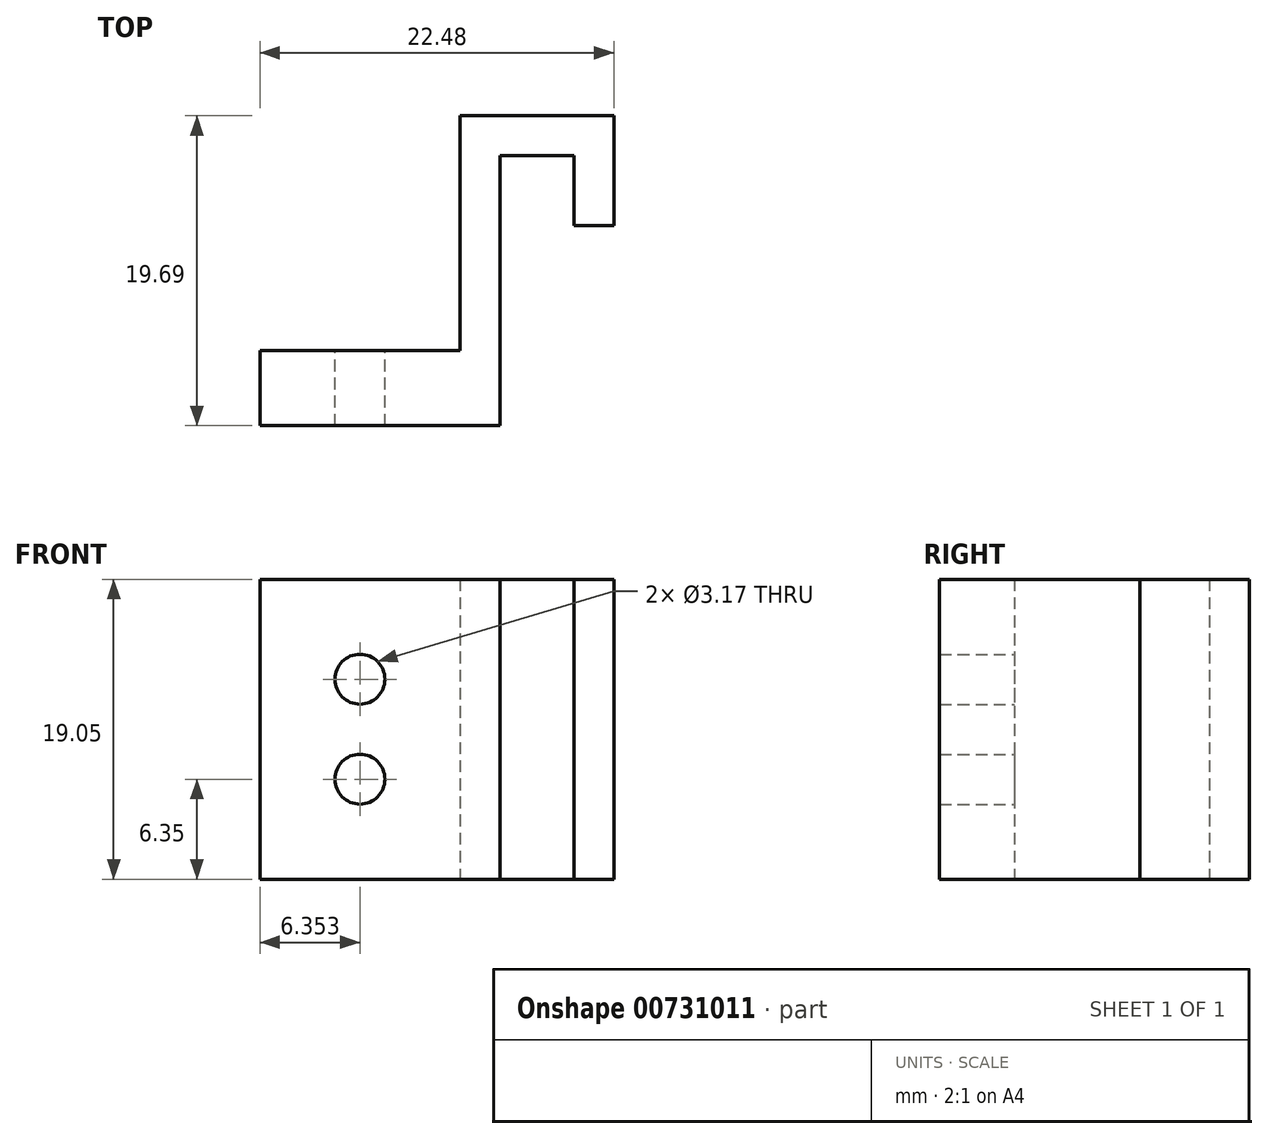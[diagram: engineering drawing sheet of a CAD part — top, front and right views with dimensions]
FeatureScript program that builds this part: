
annotation { "Feature Type Name" : "Feature", "Feature Type Description" : "" }
export const myFeature = defineFeature(function(context is Context, id is Id, definition is map)
    precondition{}
    {
        {
            var Q0;
            Q0=qCreatedBy(makeId("Top.planeOp"),FACE);
            var sketch = newSketch(context, id + "F0", { "sketchPlane" : qUnion([Q0])});
            skLineSegment(sketch, "E0.bottom", {"start": v(0, 0) * mm, "end": v(7.24, 0) * mm});
            skLineSegment(sketch, "E0.top", {"start": v(0, 2.54) * mm, "end": v(7.24, 2.54) * mm});
            skLineSegment(sketch, "E0.left", {"start": v(0, 0) * mm, "end": v(0, 2.54) * mm});
            skLineSegment(sketch, "E0.right", {"start": v(7.24, 0) * mm, "end": v(7.24, 2.54) * mm});
            skLineSegment(sketch, "E1.bottom", {"start": v(7.24, 0) * mm, "end": v(4.7, 0) * mm});
            skLineSegment(sketch, "E1.top", {"start": v(7.24, -4.42) * mm, "end": v(4.7, -4.42) * mm});
            skLineSegment(sketch, "E1.left", {"start": v(7.24, 0) * mm, "end": v(7.24, -4.42) * mm});
            skLineSegment(sketch, "E1.right", {"start": v(4.7, 0) * mm, "end": v(4.7, -4.42) * mm});
            skLineSegment(sketch, "E2.bottom", {"start": v(0, 2.54) * mm, "end": v(-2.54, 2.54) * mm});
            skLineSegment(sketch, "E2.top", {"start": v(0, -17.15) * mm, "end": v(-2.54, -17.15) * mm});
            skLineSegment(sketch, "E2.left", {"start": v(0, 2.54) * mm, "end": v(0, -17.15) * mm});
            skLineSegment(sketch, "E2.right", {"start": v(-2.54, 2.54) * mm, "end": v(-2.54, -17.15) * mm});
            skLineSegment(sketch, "E3.bottom", {"start": v(-2.54, -17.15) * mm, "end": v(-15.24, -17.15) * mm});
            skLineSegment(sketch, "E3.top", {"start": v(-2.54, -12.38) * mm, "end": v(-15.24, -12.38) * mm});
            skLineSegment(sketch, "E3.left", {"start": v(-2.54, -17.15) * mm, "end": v(-2.54, -12.38) * mm});
            skLineSegment(sketch, "E3.right", {"start": v(-15.24, -17.15) * mm, "end": v(-15.24, -12.38) * mm});
            skSolve(sketch);
        }
        {
            var Q0;
            Q0 = qSketchRegion(id + "F0", true);
            extrude(context, id + "F1", {"entities" : qUnion([Q0]), "depth" : 19.05 * mm, "offsetDistance" : 25.4 * mm});
        }
        {
            var Q0;
            Q0=qCreatedBy(makeId("Front.planeOp"),FACE);
            cPlane(context, id + "F2", {"entities" : qUnion([Q0]), "cplaneType" : CPlaneType.OFFSET, "offset" : 12.38 * mm, "width" : 152.4 * mm, "height" : 152.4 * mm});
        }
        {
            var Q0;
            Q0=qCreatedBy(id+"F2.planeOp",FACE);
            var sketch = newSketch(context, id + "F3", { "sketchPlane" : qUnion([Q0])});
            skPoint(sketch, "E4", {"position": v(-8.89, 12.7) * mm});
            skPoint(sketch, "E5", {"position": v(-8.89, 6.35) * mm});
            skSolve(sketch);
        }
        {
            var Q0;
            Q0=sQuery(id+"F3.wireOp",VERTEX,"E4");
            var Q1;
            Q1=sQuery(id+"F3.wireOp",VERTEX,"E5");
            var Q2;
            Q2=makeQuery(id+"F1.opExtrude","SWEPT_BODY",BODY,{"disambiguationData":[OSD([sQuery(id+"F0.wireOp",EDGE,"E0.bottom"),sQuery(id+"F0.wireOp",EDGE,"E0.top"),sQuery(id+"F0.wireOp",EDGE,"E0.right"),sQuery(id+"F0.wireOp",EDGE,"E1.top"),sQuery(id+"F0.wireOp",EDGE,"E1.left"),sQuery(id+"F0.wireOp",EDGE,"E1.right"),sQuery(id+"F0.wireOp",EDGE,"E2.bottom"),sQuery(id+"F0.wireOp",EDGE,"E2.top"),sQuery(id+"F0.wireOp",EDGE,"E2.left"),sQuery(id+"F0.wireOp",EDGE,"E2.right"),sQuery(id+"F0.wireOp",EDGE,"E3.bottom"),sQuery(id+"F0.wireOp",EDGE,"E3.top"),sQuery(id+"F0.wireOp",EDGE,"E3.right")])]});
            hole(context, id + "F4", {"style" : HoleStyle.SIMPLE, "endStyle" : HoleEndStyle.THROUGH, "oppositeDirection" : true, "holeDiameter" : 3.17 * mm, "majorDiameter" : 6.35 * mm, "isTappedThrough" : true, "tappedDepth" : 12.7 * mm, "tapClearance" : 3, "locations" : qUnion([Q0, Q1]), "scope" : qUnion([Q2])});
        }
    });
